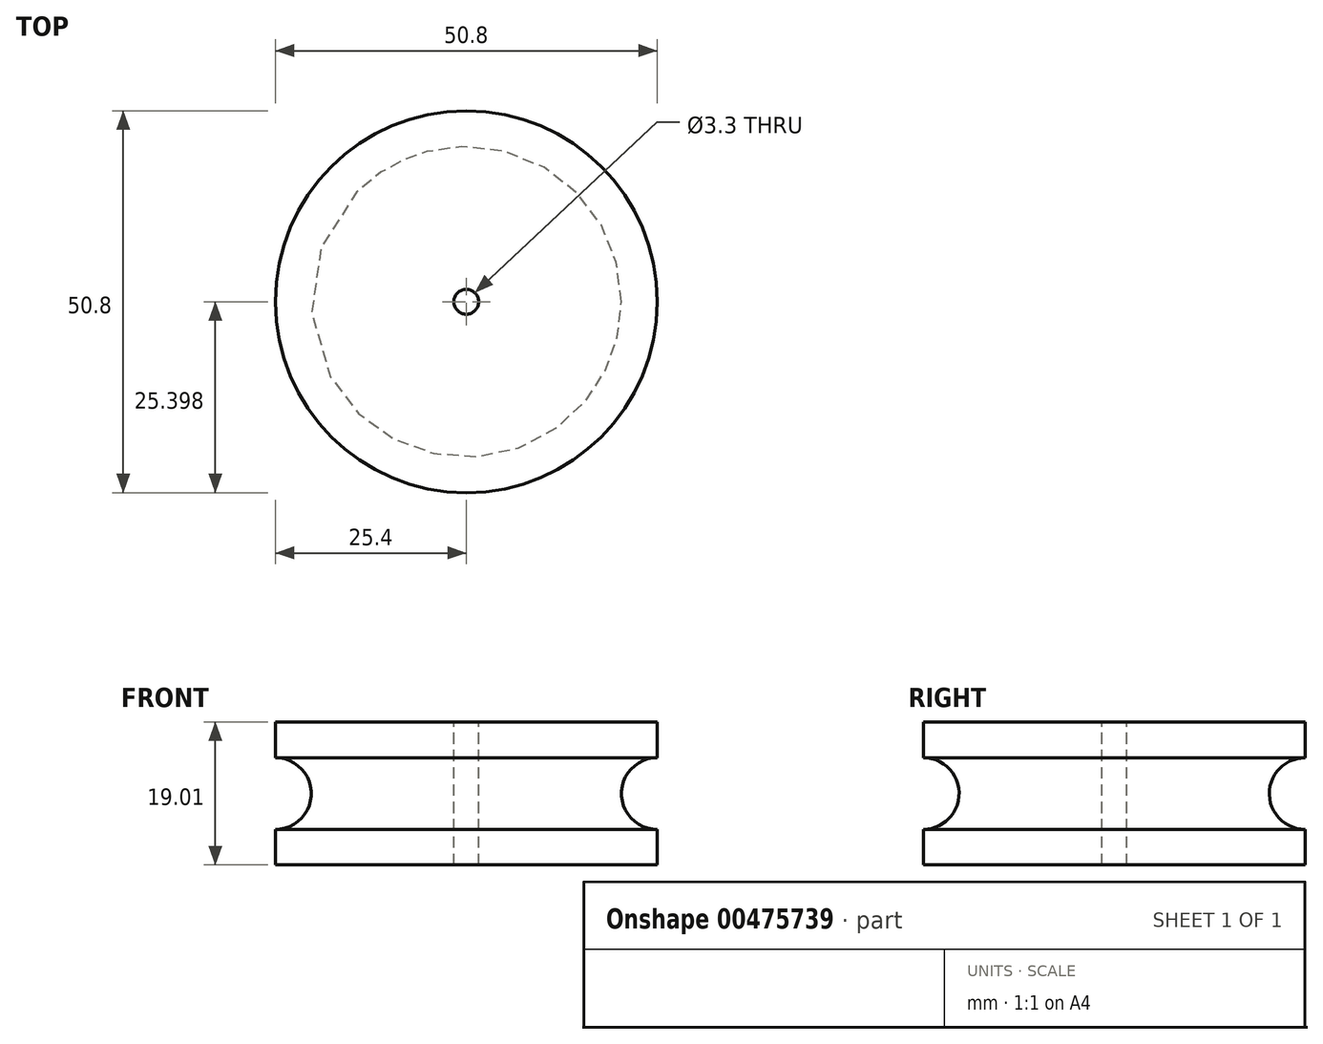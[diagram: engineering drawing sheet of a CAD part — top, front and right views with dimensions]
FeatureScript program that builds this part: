
annotation { "Feature Type Name" : "Feature", "Feature Type Description" : "" }
export const myFeature = defineFeature(function(context is Context, id is Id, definition is map)
    precondition{}
    {
        {
            var Q0;
            Q0=qCreatedBy(makeId("Right.planeOp"),FACE);
            var sketch = newSketch(context, id + "F0", { "sketchPlane" : qUnion([Q0])});
            skLineSegment(sketch, "E0.bottom", {"start": v(-37.33, 19) * mm, "end": v(-11.93, 19) * mm});
            skLineSegment(sketch, "E0.top", {"start": v(-37.33, 0) * mm, "end": v(-11.93, 0) * mm});
            skLineSegment(sketch, "E0.left", {"start": v(-37.33, 19) * mm, "end": v(-37.33, 0) * mm});
            skLineSegment(sketch, "E0.right", {"start": v(-11.93, 19) * mm, "end": v(-11.93, 0) * mm});
            skCircle(sketch, "E1", {"center": v(-11.93, 9.5) * mm, "radius": 4.76 * mm});
            skSolve(sketch);
        }
        {
            var Q0;
            {var subQ1=sQuery(id+"F0.wireOp",EDGE,"E0.bottom");Q0=makeQuery(id+"F0.imprint","IMPRINT",FACE,{"disambiguationData":[TD([[makeQuery(id+"F0.imprint","IMPRINT",EDGE,{"derivedFrom":subQ1}),-1.0]])]});}
            var Q1;
            Q1=sQuery(id+"F0.wireOp",EDGE,"E0.left");
            revolve(context, id + "F1", {"entities" : qUnion([Q0]), "axis" : qUnion([Q1]), "revolveType" : RevolveType.FULL});
        }
        {
            var Q0;
            Q0=makeQuery(id+"F1.opRevolve","SWEPT_FACE",FACE,{"disambiguationData":[OSD([sQuery(id+"F0.wireOp",EDGE,"E0.bottom")])]});
            var sketch = newSketch(context, id + "F2", { "sketchPlane" : qUnion([Q0])});
            skCircle(sketch, "E2", {"center": v(0, -37.33) * mm, "radius": 1.65 * mm});
            skSolve(sketch);
        }
        {
            var Q0;
            Q0 = qSketchRegion(id + "F2", true);
            extrude(context, id + "F3", {"entities" : qUnion([Q0]), "operationType" : NewBodyOperationType.REMOVE, "oppositeDirection" : true, "depth" : 25.4 * mm, "offsetDistance" : 25.4 * mm});
        }
    });
